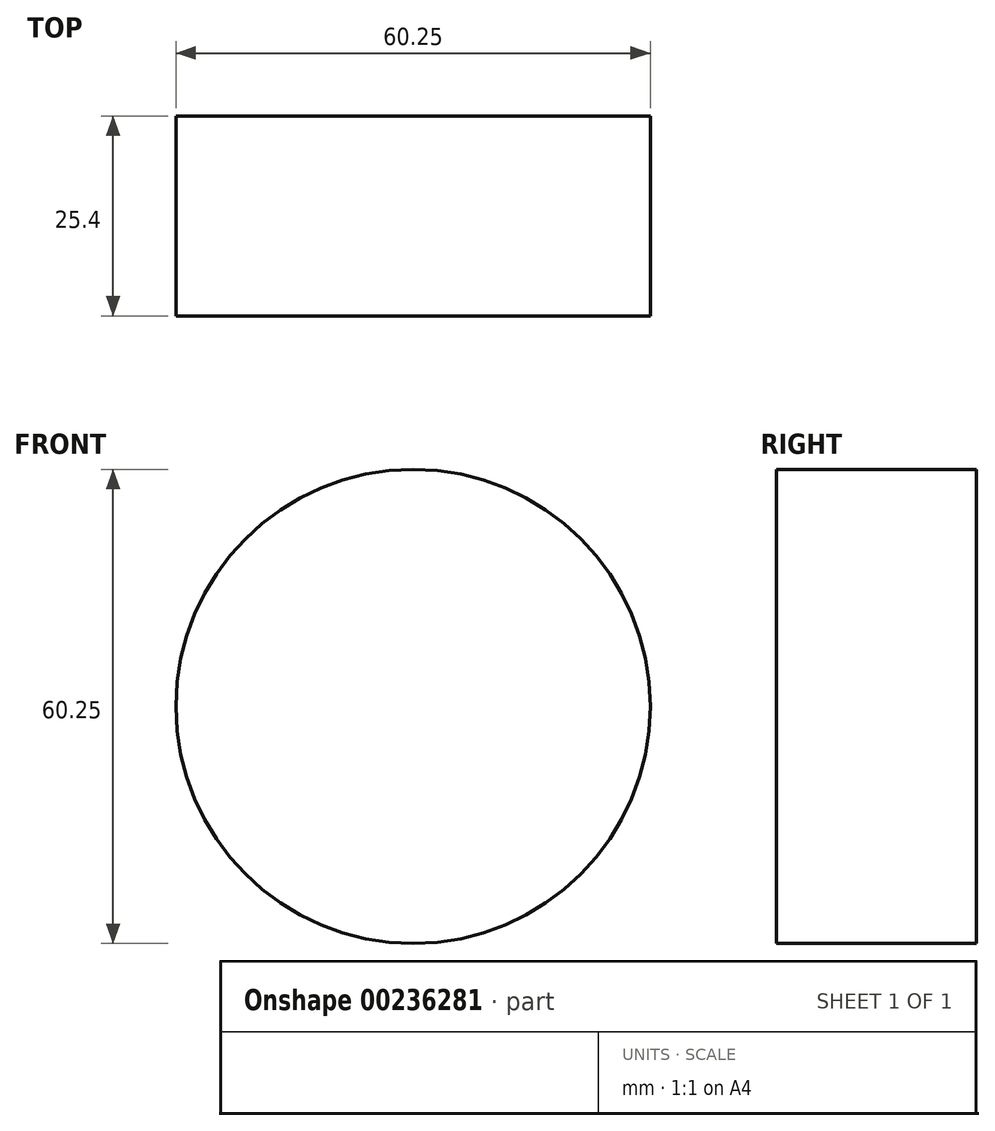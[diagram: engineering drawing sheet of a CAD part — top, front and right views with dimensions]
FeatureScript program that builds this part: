
annotation { "Feature Type Name" : "Feature", "Feature Type Description" : "" }
export const myFeature = defineFeature(function(context is Context, id is Id, definition is map)
    precondition{}
    {
        {
            var Q0;
            Q0=qCreatedBy(makeId("Front.planeOp"),FACE);
            var sketch = newSketch(context, id + "F0", { "sketchPlane" : qUnion([Q0])});
            skCircle(sketch, "E0", {"center": v(-30.79, 34.64) * mm, "radius": 30.12 * mm});
            skSolve(sketch);
        }
        {
            var Q0;
            Q0=makeQuery(id+"F0.imprint","IMPRINT",FACE,{"disambiguationData":[TD([[makeQuery(id+"F0.imprint","IMPRINT",EDGE,{"derivedFrom":sQuery(id+"F0.wireOp",EDGE,"E0")}),1.0]])]});
            var Q1;
            Q1=sQuery(id+"F0.wireOp",EDGE,"E0");
            extrude(context, id + "F1", {"entities" : qUnion([Q0]), "surfaceEntities" : qUnion([Q1]), "oppositeDirection" : true, "depth" : 25.4 * mm});
        }
    });
